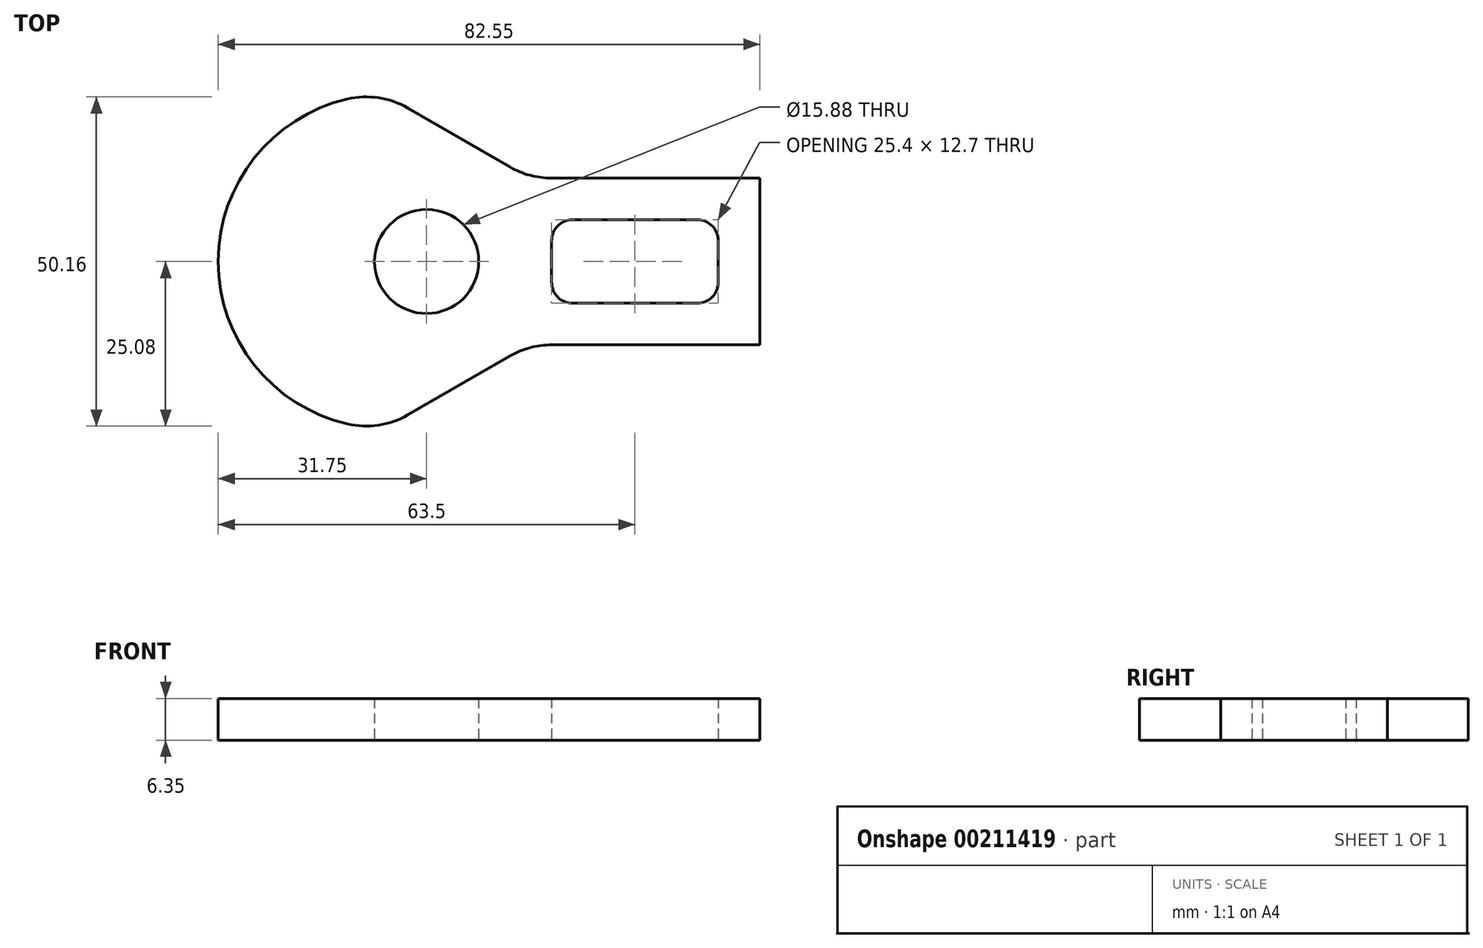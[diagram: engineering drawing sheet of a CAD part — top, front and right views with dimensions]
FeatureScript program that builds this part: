
annotation { "Feature Type Name" : "Feature", "Feature Type Description" : "" }
export const myFeature = defineFeature(function(context is Context, id is Id, definition is map)
    precondition{}
    {
        {
            var Q0;
            Q0=qCreatedBy(makeId("Top.planeOp"),FACE);
            var sketch = newSketch(context, id + "F0", { "sketchPlane" : qUnion([Q0])});
            skLineSegment(sketch, "E0.bottom", {"start": v(12.7, 12.7) * mm, "end": v(44.45, 12.7) * mm});
            skLineSegment(sketch, "E0.top", {"start": v(12.7, -12.7) * mm, "end": v(44.45, -12.7) * mm});
            skLineSegment(sketch, "E0.right", {"start": v(44.45, 12.7) * mm, "end": v(44.45, -12.7) * mm});
            skArc(sketch, "E1", {"start": v(-18.39, 24.75) * mm, "mid": v(-38.1, 0) * mm, "end": v(-18.39, -24.75) * mm});
            skLineSegment(sketch, "E2", {"start": v(6.35, 14.4) * mm, "end": v(-9.2, 23.38) * mm});
            skLineSegment(sketch, "E3", {"start": v(-9.2, -23.38) * mm, "end": v(6.35, -14.4) * mm});
            skPoint(sketch, "E4.visualSharp", {"position": v(9.3, 12.7) * mm});
            skArc(sketch, "E4.filletArc", {"start": v(6.35, 14.4) * mm, "mid": v(9.41, 13.13) * mm, "end": v(12.7, 12.7) * mm});
            skPoint(sketch, "E5.visualSharp", {"position": v(-12.7, 25.4) * mm});
            skArc(sketch, "E5.filletArc", {"start": v(-9.2, 23.38) * mm, "mid": v(-13.66, 24.94) * mm, "end": v(-18.39, 24.75) * mm});
            skPoint(sketch, "E6.visualSharp", {"position": v(9.3, -12.7) * mm});
            skArc(sketch, "E6.filletArc", {"start": v(12.7, -12.7) * mm, "mid": v(9.41, -13.13) * mm, "end": v(6.35, -14.4) * mm});
            skPoint(sketch, "E7.visualSharp", {"position": v(-12.7, -25.4) * mm});
            skArc(sketch, "E7.filletArc", {"start": v(-18.39, -24.75) * mm, "mid": v(-13.66, -24.94) * mm, "end": v(-9.2, -23.38) * mm});
            skLineSegment(sketch, "E8.bottom", {"start": v(34.93, 6.35) * mm, "end": v(15.87, 6.35) * mm});
            skLineSegment(sketch, "E8.top", {"start": v(34.93, -6.35) * mm, "end": v(15.87, -6.35) * mm});
            skLineSegment(sketch, "E8.left", {"start": v(38.1, 3.18) * mm, "end": v(38.1, -3.17) * mm});
            skLineSegment(sketch, "E8.right", {"start": v(12.7, 3.17) * mm, "end": v(12.7, -3.18) * mm});
            skPoint(sketch, "E9.visualSharp", {"position": v(12.7, 6.35) * mm});
            skArc(sketch, "E9.filletArc", {"start": v(15.87, 6.35) * mm, "mid": v(13.63, 5.42) * mm, "end": v(12.7, 3.17) * mm});
            skPoint(sketch, "E10.visualSharp", {"position": v(12.7, -6.35) * mm});
            skArc(sketch, "E10.filletArc", {"start": v(12.7, -3.18) * mm, "mid": v(13.63, -5.42) * mm, "end": v(15.87, -6.35) * mm});
            skPoint(sketch, "E11.visualSharp", {"position": v(38.1, 6.35) * mm});
            skArc(sketch, "E11.filletArc", {"start": v(38.1, 3.18) * mm, "mid": v(37.17, 5.42) * mm, "end": v(34.93, 6.35) * mm});
            skPoint(sketch, "E12.visualSharp", {"position": v(38.1, -6.35) * mm});
            skArc(sketch, "E12.filletArc", {"start": v(34.93, -6.35) * mm, "mid": v(37.17, -5.42) * mm, "end": v(38.1, -3.17) * mm});
            skCircle(sketch, "E13", {"center": v(-6.35, 0) * mm, "radius": 7.94 * mm});
            skSolve(sketch);
        }
        {
            var Q0;
            Q0 = qSketchRegion(id + "F0", true);
            extrude(context, id + "F1", {"entities" : qUnion([Q0]), "depth" : 6.35 * mm});
        }
    });
